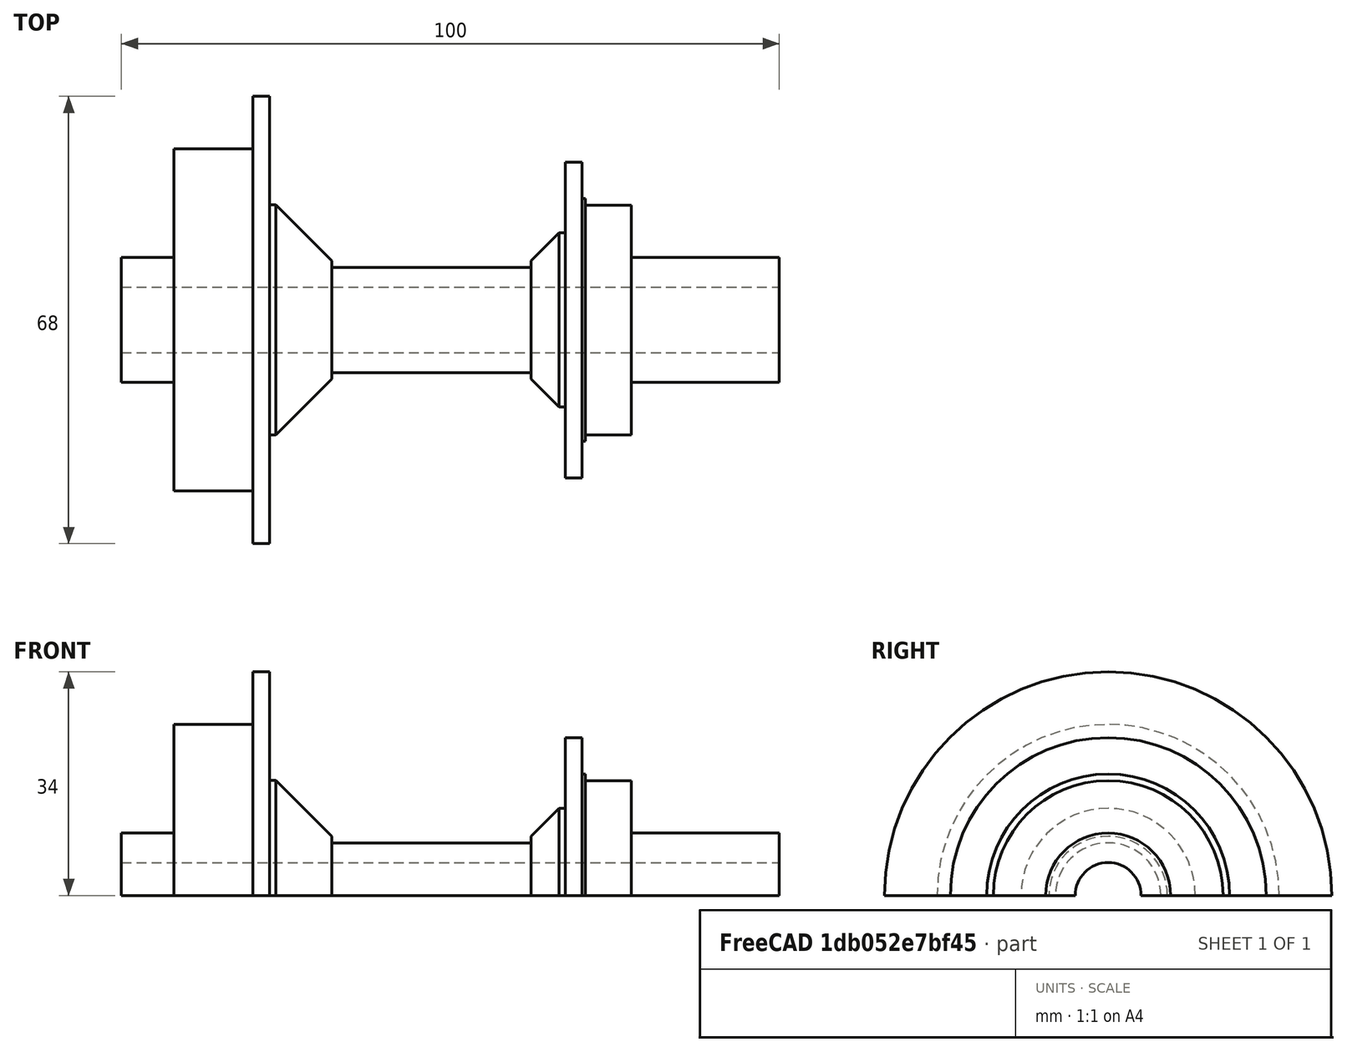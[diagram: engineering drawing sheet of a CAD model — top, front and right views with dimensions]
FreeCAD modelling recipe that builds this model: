
FCSTD DOCUMENT  (FreeCAD 0.16R)
Label: 100mmMTB_wChainline
License: All rights reserved
LicenseURL: http://en.wikipedia.org/wiki/All_rights_reserved
objects: Sketcher::SketchObject×1, PartDesign::Revolution×1
note: 3 computed .brp shape members not serialized (recipe doc carries the construction recipe); baked Part::Feature solids carry a one-line shape summary decoded from their .brp

FEATURE [Sketcher::SketchObject] Sketch
  sketch-geometry (52):
    g0: LineSegment StartX=26.5 StartY=9.5 StartZ=0 EndX=26.5 EndY=17.46 EndZ=0
    g1: LineSegment StartX=26.5 StartY=17.46 StartZ=0 EndX=19.5 EndY=17.46 EndZ=0
    g2: LineSegment StartX=19.5 StartY=18.46 StartZ=0 EndX=19 EndY=18.46 EndZ=0
    g3: LineSegment StartX=19 StartY=18.46 StartZ=0 EndX=19 EndY=24 EndZ=0
    g4: LineSegment StartX=19 StartY=24 StartZ=0 EndX=16.5 EndY=24 EndZ=0
    g5: LineSegment StartX=16.5 StartY=24 StartZ=0 EndX=16.5 EndY=13.2426 EndZ=0
    g6: LineSegment StartX=16.5 StartY=13.2426 StartZ=0 EndX=15.5 EndY=13.2426 EndZ=0
    g7: LineSegment StartX=15.5 StartY=13.2426 StartZ=0 EndX=11.2574 EndY=9 EndZ=0
    g8: LineSegment StartX=11.2574 StartY=8 StartZ=0 EndX=-16.0147 EndY=8 EndZ=0
    g9: LineSegment StartX=-25.5 StartY=17.4853 StartZ=0 EndX=-25.5 EndY=34 EndZ=0
    g10: LineSegment StartX=-25.5 StartY=34 StartZ=0 EndX=-28 EndY=34 EndZ=0
    g11: LineSegment StartX=-28 StartY=34 StartZ=0 EndX=-28 EndY=26 EndZ=0
    g12: LineSegment StartX=-44 StartY=26 StartZ=0 EndX=-44 EndY=9.5 EndZ=0
    g13: LineSegment StartX=-24.5 StartY=17.4853 StartZ=0 EndX=-16.0147 EndY=9 EndZ=0
    g14: LineSegment StartX=-25.5 StartY=17.4853 StartZ=0 EndX=-24.5 EndY=17.4853 EndZ=0
    g15: LineSegment StartX=-16.0147 StartY=9 StartZ=0 EndX=-16.0147 EndY=8 EndZ=0
    g16: LineSegment StartX=11.2574 StartY=9 StartZ=0 EndX=11.2574 EndY=8 EndZ=0
    g17: LineSegment StartX=19.5 StartY=18.46 StartZ=0 EndX=19.5 EndY=17.46 EndZ=0
    g18: LineSegment StartX=-44 StartY=26 StartZ=0 EndX=-28 EndY=26 EndZ=0
    g19: LineSegment [constr] StartX=22 StartY=55 StartZ=0 EndX=22 EndY=20 EndZ=0
    g20: LineSegment [constr] StartX=27.5 StartY=45 StartZ=0 EndX=27.5 EndY=20 EndZ=0
    g21: LineSegment [constr] StartX=33 StartY=33 StartZ=0 EndX=33 EndY=20 EndZ=0
    g22: LineSegment [constr] StartX=38.5 StartY=28 StartZ=0 EndX=38.5 EndY=20 EndZ=0
    g23: LineSegment [constr] StartX=44 StartY=22.5 StartZ=0 EndX=44 EndY=9.5 EndZ=0
    g24: LineSegment StartX=-50 StartY=5 StartZ=0 EndX=-50 EndY=9.5 EndZ=0
    g25: LineSegment [constr] StartX=-45.6 StartY=60 StartZ=0 EndX=-44 EndY=60 EndZ=0
    g26: LineSegment [constr] StartX=-44 StartY=60 StartZ=0 EndX=-44 EndY=20 EndZ=0
    g27: LineSegment [constr] StartX=-44 StartY=20 StartZ=0 EndX=-45.6 EndY=20 EndZ=0
    g28: LineSegment [constr] StartX=-45.6 StartY=20 StartZ=0 EndX=-45.6 EndY=60 EndZ=0
    g29: LineSegment [constr] StartX=0 StartY=0 StartZ=0 EndX=0 EndY=193 EndZ=0
    g30: LineSegment [constr] StartX=-28 StartY=34 StartZ=0 EndX=0 EndY=193 EndZ=0
    g31: LineSegment [constr] StartX=19 StartY=24 StartZ=0 EndX=0 EndY=193 EndZ=0
    g32: LineSegment StartX=26.5 StartY=9.5 StartZ=0 EndX=50 EndY=9.5 EndZ=0
    g33: LineSegment StartX=50 StartY=9.5 StartZ=0 EndX=50 EndY=5 EndZ=0
    g34: LineSegment StartX=-50 StartY=5 StartZ=0 EndX=50 EndY=5 EndZ=0
    g35: LineSegment StartX=-44 StartY=9.5 StartZ=0 EndX=-50 EndY=9.5 EndZ=0
    g36: Circle [constr] CenterX=0 CenterY=224 CenterZ=0 NormalX=0 NormalY=0 NormalZ=1 Radius=26
    g37: LineSegment [constr] StartX=-25 StartY=296 StartZ=0 EndX=25 EndY=296 EndZ=0
    g38: LineSegment [constr] StartX=25 StartY=264 StartZ=0 EndX=-25 EndY=264 EndZ=0
    g39: LineSegment [constr] StartX=-25 StartY=264 StartZ=0 EndX=-25 EndY=296 EndZ=0
    g40: LineSegment [constr] StartX=35 StartY=344 StartZ=0 EndX=38 EndY=344 EndZ=0
    g41: LineSegment [constr] StartX=38 StartY=344 StartZ=0 EndX=38 EndY=216 EndZ=0
    g42: LineSegment [constr] StartX=38 StartY=216 StartZ=0 EndX=35 EndY=216 EndZ=0
    g43: LineSegment [constr] StartX=25 StartY=296 StartZ=0 EndX=25 EndY=280 EndZ=0
    g44: LineSegment [constr] StartX=25 StartY=280 StartZ=0 EndX=25 EndY=264 EndZ=0
    g45: LineSegment [constr] StartX=35 StartY=344 StartZ=0 EndX=35 EndY=280 EndZ=0
    g46: LineSegment [constr] StartX=35 StartY=280 StartZ=0 EndX=35 EndY=216 EndZ=0
    g47: LineSegment [constr] StartX=25 StartY=280 StartZ=0 EndX=105 EndY=280 EndZ=0
    g48: LineSegment [constr] StartX=-44 StartY=60 StartZ=0 EndX=-44 EndY=42 EndZ=0
    g49: LineSegment [constr] StartX=-44 StartY=60 StartZ=0 EndX=-28 EndY=60 EndZ=0
    g50: LineSegment [constr] StartX=-28 StartY=60 StartZ=0 EndX=-28 EndY=42 EndZ=0
    g51: LineSegment [constr] StartX=-28 StartY=42 StartZ=0 EndX=-44 EndY=42 EndZ=0
  constraints (160):
    c: Coincident(g2,g3)
    c: Vertical(g3)
    c: Coincident(g3,g4)
    c: Horizontal(g4)
    c: Coincident(g4,g5)
    c: Vertical(g5)
    c: Coincident(g5,g6)
    c: Coincident(g6,g7)
    c: Horizontal(g8)
    c: Vertical(g9)
    c: Coincident(g9,g10)
    c: Horizontal(g6)
    c: Horizontal(g1)
    c: Horizontal(g10)
    c: DistanceY(g-1,g0) = 9.5
    c: Vertical(g0)
    c: DistanceX(g2,g2) = 0.5
    c: Horizontal(g2)
    c: DistanceY(g-1,g1) = 17.46
    c: DistanceX(g4,g4) = 2.5
    c: DistanceX(g1,g1) = 7
    c: DistanceY(g1,g2) = 1
    c: DistanceY(g-1,g8) = 8
    c: DistanceX(g10,g10) = 2.5
    c: DistanceY(g-1,g4) = 24
    c: Distance(g6) = 1
    c: Angle(g7) = -2.35619
    c: Distance(g7) = 6
    c: Coincident(g10,g11)
    c: Vertical(g12)
    c: Vertical(g11)
    c: DistanceY(g10) = 34
    c: DistanceY(g12) = 26
    c: DistanceX(g12,g11) = 16
    c: Angle(g13) = -0.785398
    c: Distance(g13) = 12
    c: Horizontal(g14)
    c: DistanceX(g14,g14) = 1
    c: Vertical(g15)
    c: Distance(g15) = 1
    c: Coincident(g15,g13)
    c: Coincident(g14,g13)
    c: Coincident(g14,g9)
    c: Coincident(g15,g8)
    c: Vertical(g16)
    c: Distance(g16) = 1
    c: Coincident(g16,g8)
    c: Coincident(g16,g7)
    c: Vertical(g17)
    c: Coincident(g17,g2)
    c: Coincident(g17,g1)
    c: Horizontal(g18)
    c: Coincident(g18,g12)
    c: Coincident(g18,g11)
    c: Vertical(g19)
    c: Vertical(g20)
    c: Vertical(g21)
    c: Vertical(g23)
    c: Vertical(g22)
    c: DistanceX(g19,g20) = 5.5
    c: DistanceX(g20,g21) = 5.5
    c: DistanceX(g21,g22) = 5.5
    c: DistanceX(g22,g23) = 5.5
    c: DistanceY(g19) = 55
    c: DistanceX(g2,g19) = 3
    c: Vertical(g24)
    c: Coincident(g25,g26)
    c: Coincident(g26,g27)
    c: Coincident(g27,g28)
    c: Coincident(g28,g25)
    c: Horizontal(g25)
    c: Horizontal(g27)
    c: Vertical(g26)
    c: Vertical(g28)
    c: DistanceX(g25,g25) = 1.6
    c: PointOnObject(g29,g-1)
    c: Vertical(g29)
    c: Distance(g29) = 193
    c: Coincident(g30,g29)
    c: Coincident(g30,g31)
    c: Coincident(g31,g3)
    c: Coincident(g30,g10)
    c: DistanceY(g22) = 20
    c: DistanceY(g21) = 20
    c: DistanceY(g20) = 20
    c: DistanceY(g19) = 20
    c: Distance(g20) = 25
    c: Distance(g22) = 8
    c: Distance(g21) = 13
    c: DistanceY(g23,g23) = 13
    c: Coincident(g1,g0)
    c: Coincident(g34,g33)
    c: Horizontal(g34)
    c: Vertical(g33)
    c: Distance(g32,g23) = 6
    c: Coincident(g33,g32)
    c: PointOnObject(g23,g32)
    c: Horizontal(g32)
    c: DistanceY(g32) = 9.5
    c: DistanceY(g33) = 5
    c: DistanceX(g24,g33) = 100
    c: DistanceX(g24,g29) = 50
    c: Coincident(g35,g12)
    c: Coincident(g35,g24)
    c: DistanceY(g26) = 20
    c: Coincident(g24,g34)
    c: Horizontal(g35)
    c: DistanceY(g12) = 9.5
    c: PointOnObject(g26,g12)
    c: DistanceX(g35,g35) = 6
    c: Coincident(g32,g0)
    c: Coincident(g-1,g29)
    c: Radius(g36) = 26
    c: PointOnObject(g36,g-2)
    c: DistanceY(g36) = 224
    c: Coincident(g38,g39)
    c: Coincident(g39,g37)
    c: Horizontal(g37)
    c: Horizontal(g38)
    c: Vertical(g39)
    c: Symmetric(g38,g38,g-2)
    c: Distance(g37) = 50
    c: Coincident(g40,g41)
    c: Coincident(g41,g42)
    c: Horizontal(g40)
    c: Horizontal(g42)
    c: Vertical(g41)
    c: Distance(g42) = 3
    c: Distance(g41) = 128
    c: Vertical(g43)
    c: Coincident(g44,g43)
    c: Coincident(g43,g37)
    c: Coincident(g44,g38)
    c: Symmetric(g37,g38,g43)
    c: Vertical(g45)
    c: Coincident(g46,g42)
    c: Coincident(g45,g40)
    c: Vertical(g46)
    c: Coincident(g46,g45)
    c: Horizontal(g47)
    c: Coincident(g47,g43)
    c: Distance(g47) = 80
    c: PointOnObject(g45,g47)
    c: DistanceX(g43,g45) = 10
    c: Vertical(g48)
    c: Horizontal(g49)
    c: Coincident(g49,g50)
    c: Coincident(g50,g51)
    c: Coincident(g51,g48)
    c: Horizontal(g51)
    c: Vertical(g50)
    c: Distance(g51) = 16
    c: Coincident(g49,g48)
    c: Distance(g50) = 18
    c: PointOnObject(g48,g26)
    c: Coincident(g48,g25)
    c: DistanceY(g25) = 60
    c: DistanceY(g43) = 280
    c: Distance(g39) = 32
    c: Symmetric(g42,g40,g47)
FEATURE [PartDesign::Revolution] Revolution
  Angle = 180
  Axis = (1,0,0)
  Base = (0,0,0)
  ReferenceAxis = -> Sketch [H_Axis]
  Sketch = -> Sketch
